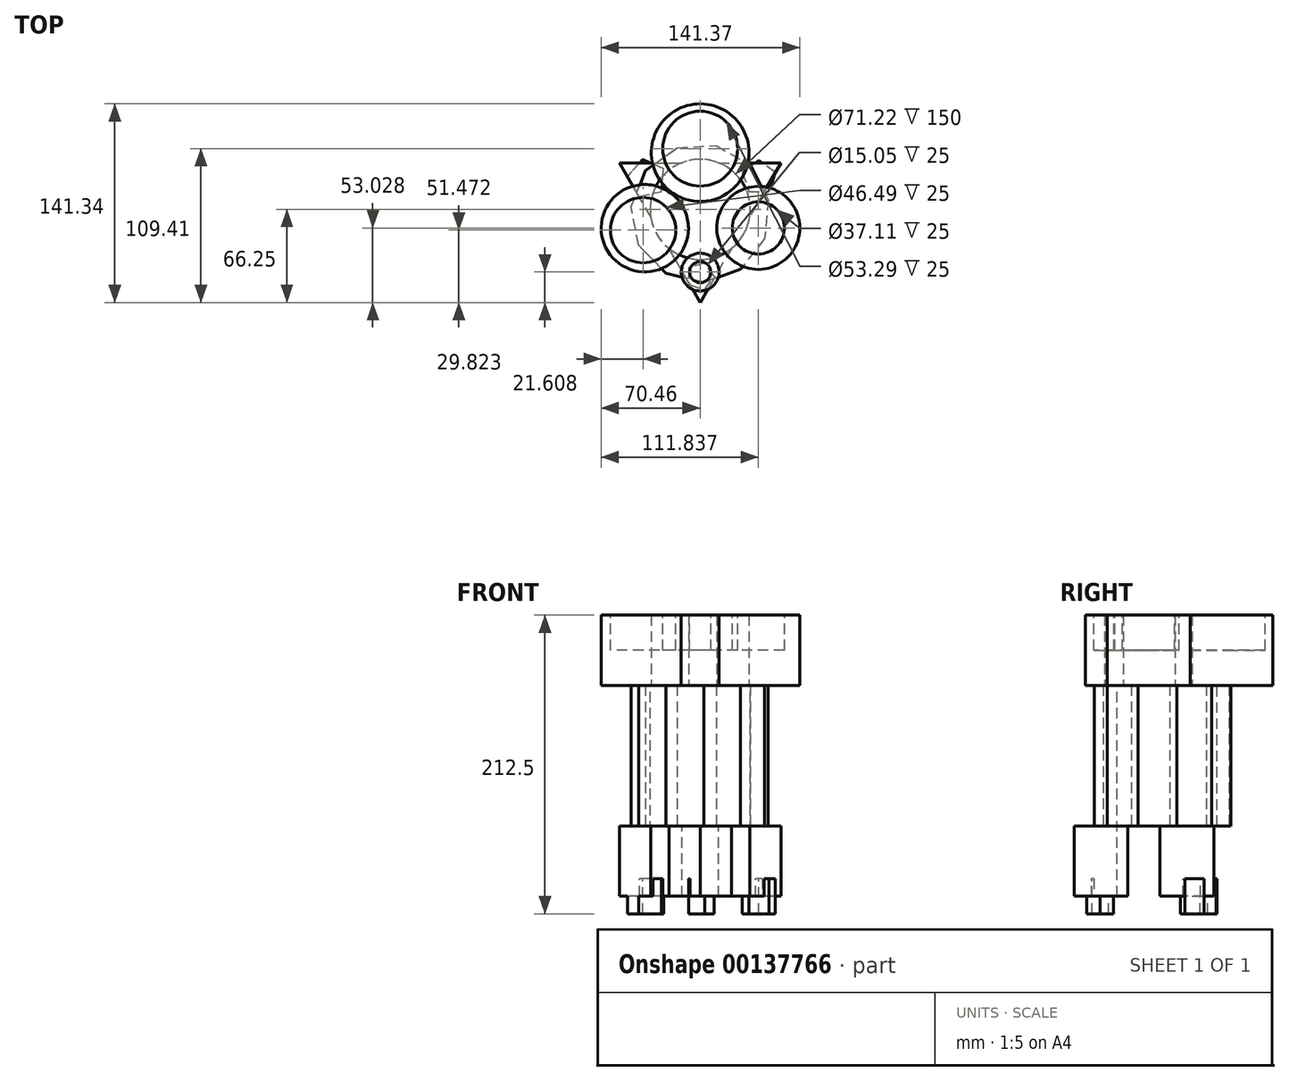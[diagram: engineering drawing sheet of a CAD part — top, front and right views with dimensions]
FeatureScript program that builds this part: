
annotation { "Feature Type Name" : "Feature", "Feature Type Description" : "" }
export const myFeature = defineFeature(function(context is Context, id is Id, definition is map)
    precondition{}
    {
        {
            var Q0;
            Q0=qCreatedBy(makeId("Top.planeOp"),FACE);
            var sketch = newSketch(context, id + "F0", { "sketchPlane" : qUnion([Q0])});
            skCircle(sketch, "E0.cCircle", {"center": v(0, 0) * mm, "radius": 33.12 * mm, "construction": true});
            skLineSegment(sketch, "E0.0", {"start": v(-57.37, 33.12) * mm, "end": v(57.37, 33.12) * mm});
            skLineSegment(sketch, "E0.1", {"start": v(57.37, 33.12) * mm, "end": v(0, -66.25) * mm});
            skLineSegment(sketch, "E0.2", {"start": v(0, -66.25) * mm, "end": v(-57.37, 33.12) * mm});
            skPoint(sketch, "E0.0.midPoint", {"position": v(0, 33.12) * mm});
            skSolve(sketch);
        }
        {
            var Q0;
            Q0 = qSketchRegion(id + "F0", true);
            extrude(context, id + "F1", {"entities" : qUnion([Q0]), "depth" : 50 * mm});
        }
        {
            var Q0;
            Q0=makeQuery(id+"F1.opExtrude","CAP_FACE",FACE,{"disambiguationData":[OSD([sQuery(id+"F0.wireOp",EDGE,"E0.0"),sQuery(id+"F0.wireOp",EDGE,"E0.1"),sQuery(id+"F0.wireOp",EDGE,"E0.2")])],"isStart":false});
            var sketch = newSketch(context, id + "F2", { "sketchPlane" : qUnion([Q0])});
            skCircle(sketch, "E1.cCircle", {"center": v(0, -2.63) * mm, "radius": 47.32 * mm, "construction": true});
            skLineSegment(sketch, "E1.0", {"start": v(11.42, 45.34) * mm, "end": v(35.54, 31.56) * mm});
            skLineSegment(sketch, "E1.1", {"start": v(35.54, 31.56) * mm, "end": v(48.38, 6.91) * mm});
            skLineSegment(sketch, "E1.2", {"start": v(48.38, 6.91) * mm, "end": v(45.86, -20.76) * mm});
            skLineSegment(sketch, "E1.3", {"start": v(45.86, -20.76) * mm, "end": v(28.78, -42.67) * mm});
            skLineSegment(sketch, "E1.4", {"start": v(28.78, -42.67) * mm, "end": v(2.56, -51.88) * mm});
            skLineSegment(sketch, "E1.5", {"start": v(2.56, -51.88) * mm, "end": v(-24.47, -45.44) * mm});
            skLineSegment(sketch, "E1.6", {"start": v(-24.47, -45.44) * mm, "end": v(-43.73, -25.42) * mm});
            skLineSegment(sketch, "E1.7", {"start": v(-43.73, -25.42) * mm, "end": v(-49.1, 1.85) * mm});
            skLineSegment(sketch, "E1.8", {"start": v(-49.1, 1.85) * mm, "end": v(-38.9, 27.69) * mm});
            skLineSegment(sketch, "E1.9", {"start": v(-38.9, 27.69) * mm, "end": v(-16.33, 43.9) * mm});
            skLineSegment(sketch, "E1.10", {"start": v(-16.33, 43.9) * mm, "end": v(11.42, 45.34) * mm});
            skPoint(sketch, "E1.0.midPoint", {"position": v(23.48, 38.45) * mm});
            skSolve(sketch);
        }
        {
            var Q0;
            Q0 = qSketchRegion(id + "F2", true);
            extrude(context, id + "F3", {"entities" : qUnion([Q0]), "operationType" : NewBodyOperationType.ADD, "depth" : 100 * mm});
        }
        {
            var Q0;
            Q0=makeQuery(id+"F3.opExtrude","CAP_FACE",FACE,{"disambiguationData":[OSD([sQuery(id+"F2.wireOp",EDGE,"E1.0"),sQuery(id+"F2.wireOp",EDGE,"E1.1"),sQuery(id+"F2.wireOp",EDGE,"E1.2"),sQuery(id+"F2.wireOp",EDGE,"E1.3"),sQuery(id+"F2.wireOp",EDGE,"E1.4"),sQuery(id+"F2.wireOp",EDGE,"E1.5"),sQuery(id+"F2.wireOp",EDGE,"E1.6"),sQuery(id+"F2.wireOp",EDGE,"E1.7"),sQuery(id+"F2.wireOp",EDGE,"E1.8"),sQuery(id+"F2.wireOp",EDGE,"E1.9"),sQuery(id+"F2.wireOp",EDGE,"E1.10")])],"isStart":false});
            var sketch = newSketch(context, id + "F4", { "sketchPlane" : qUnion([Q0])});
            skCircle(sketch, "E2", {"center": v(0, 0) * mm, "radius": 35.61 * mm});
            skSolve(sketch);
        }
        {
            var Q0;
            Q0 = qSketchRegion(id + "F4", true);
            extrude(context, id + "F5", {"entities" : qUnion([Q0]), "operationType" : NewBodyOperationType.REMOVE, "endBound" : BoundingType.THROUGH_ALL, "oppositeDirection" : true, "depth" : 25 * mm});
        }
        {
            var Q0;
            Q0=makeQuery(id+"F3.opExtrude","CAP_FACE",FACE,{"disambiguationData":[OSD([sQuery(id+"F2.wireOp",EDGE,"E1.0"),sQuery(id+"F2.wireOp",EDGE,"E1.1"),sQuery(id+"F2.wireOp",EDGE,"E1.2"),sQuery(id+"F2.wireOp",EDGE,"E1.3"),sQuery(id+"F2.wireOp",EDGE,"E1.4"),sQuery(id+"F2.wireOp",EDGE,"E1.5"),sQuery(id+"F2.wireOp",EDGE,"E1.6"),sQuery(id+"F2.wireOp",EDGE,"E1.7"),sQuery(id+"F2.wireOp",EDGE,"E1.8"),sQuery(id+"F2.wireOp",EDGE,"E1.9"),sQuery(id+"F2.wireOp",EDGE,"E1.10")])],"isStart":false});
            var sketch = newSketch(context, id + "F6", { "sketchPlane" : qUnion([Q0])});
            skCircle(sketch, "E3", {"center": v(0, 40.32) * mm, "radius": 34.76 * mm});
            skCircle(sketch, "E4", {"center": v(0, -44.64) * mm, "radius": 13.46 * mm});
            skCircle(sketch, "E5", {"center": v(41.38, -13.22) * mm, "radius": 29.53 * mm});
            skCircle(sketch, "E6", {"center": v(-39.39, -13.44) * mm, "radius": 31.07 * mm});
            skSolve(sketch);
        }
        {
            var Q0;
            Q0 = qSketchRegion(id + "F6", true);
            extrude(context, id + "F7", {"entities" : qUnion([Q0]), "operationType" : NewBodyOperationType.ADD, "depth" : 50 * mm});
        }
        {
            var Q0;
            {var subQ0=sQuery(id+"F0.wireOp",EDGE,"E0.0");var subQ1=sQuery(id+"F0.wireOp",EDGE,"E0.2");Q0=makeQuery(id+"F5.boolean.opBoolean","SPLIT",FACE,{"disambiguationData":[TD([makeQuery(id+"F1.opExtrude","SWEPT_FACE",FACE,{"disambiguationData":[OSD([subQ0])]}),makeQuery(id+"F1.opExtrude","SWEPT_FACE",FACE,{"disambiguationData":[OSD([subQ1])]}),makeQuery(id+"F5.opExtrude","SWEPT_FACE",FACE,{"disambiguationData":[OSD([sQuery(id+"F4.wireOp",EDGE,"E2")])]})])],"derivedFrom":makeQuery(id+"F1.opExtrude","CAP_FACE",FACE,{"disambiguationData":[OSD([subQ0,sQuery(id+"F0.wireOp",EDGE,"E0.1"),subQ1])],"isStart":true})});}
            var sketch = newSketch(context, id + "F8", { "sketchPlane" : qUnion([Q0])});
            skCircle(sketch, "E7.cCircle", {"center": v(-37.98, -21.98) * mm, "radius": 11.22 * mm, "construction": true});
            skLineSegment(sketch, "E7.0", {"start": v(-51.78, -23.43) * mm, "end": v(-43.62, -9.3) * mm});
            skLineSegment(sketch, "E7.1", {"start": v(-43.62, -9.3) * mm, "end": v(-27.67, -12.7) * mm});
            skLineSegment(sketch, "E7.2", {"start": v(-27.67, -12.7) * mm, "end": v(-25.96, -28.92) * mm});
            skLineSegment(sketch, "E7.3", {"start": v(-25.96, -28.92) * mm, "end": v(-40.86, -35.55) * mm});
            skLineSegment(sketch, "E7.4", {"start": v(-40.86, -35.55) * mm, "end": v(-51.78, -23.43) * mm});
            skPoint(sketch, "E7.0.midPoint", {"position": v(-47.7, -16.37) * mm});
            skCircle(sketch, "E8.cCircle", {"center": v(0, 47.58) * mm, "radius": 8.12 * mm, "construction": true});
            skLineSegment(sketch, "E8.0", {"start": v(-8.12, 41.68) * mm, "end": v(-8.12, 53.49) * mm});
            skLineSegment(sketch, "E8.1", {"start": v(-8.12, 53.49) * mm, "end": v(3.1, 57.13) * mm});
            skLineSegment(sketch, "E8.2", {"start": v(3.1, 57.13) * mm, "end": v(10.04, 47.58) * mm});
            skLineSegment(sketch, "E8.3", {"start": v(10.04, 47.58) * mm, "end": v(3.1, 38.03) * mm});
            skLineSegment(sketch, "E8.4", {"start": v(3.1, 38.03) * mm, "end": v(-8.12, 41.68) * mm});
            skPoint(sketch, "E8.0.midPoint", {"position": v(-8.12, 47.58) * mm});
            skCircle(sketch, "E9.cCircle", {"center": v(41.77, -22.56) * mm, "radius": 9.98 * mm, "construction": true});
            skLineSegment(sketch, "E9.0", {"start": v(34.52, -12.58) * mm, "end": v(49.03, -12.58) * mm});
            skLineSegment(sketch, "E9.1", {"start": v(49.03, -12.58) * mm, "end": v(53.5, -26.37) * mm});
            skLineSegment(sketch, "E9.2", {"start": v(53.5, -26.37) * mm, "end": v(41.77, -34.9) * mm});
            skLineSegment(sketch, "E9.3", {"start": v(41.77, -34.9) * mm, "end": v(30.04, -26.37) * mm});
            skLineSegment(sketch, "E9.4", {"start": v(30.04, -26.37) * mm, "end": v(34.52, -12.58) * mm});
            skPoint(sketch, "E9.0.midPoint", {"position": v(41.77, -12.58) * mm});
            skSolve(sketch);
        }
        {
            var Q0;
            Q0 = qSketchRegion(id + "F8", true);
            extrude(context, id + "F9", {"entities" : qUnion([Q0]), "operationType" : NewBodyOperationType.ADD, "endBound" : BoundingType.SYMMETRIC, "depth" : 25 * mm});
        }
        {
            var Q0;
            Q0=makeQuery(id+"F7.opExtrude","CAP_FACE",FACE,{"disambiguationData":[OSD([sQuery(id+"F6.wireOp",EDGE,"E4")])],"isStart":false});
            var sketch = newSketch(context, id + "F10", { "sketchPlane" : qUnion([Q0])});
            skCircle(sketch, "E10", {"center": v(0, -44.64) * mm, "radius": 7.52 * mm});
            skSolve(sketch);
        }
        {
            var Q0;
            Q0 = qSketchRegion(id + "F10", true);
            extrude(context, id + "F11", {"entities" : qUnion([Q0]), "operationType" : NewBodyOperationType.REMOVE, "oppositeDirection" : true, "depth" : 25 * mm});
        }
        {
            var Q0;
            Q0=makeQuery(id+"F7.opExtrude","CAP_FACE",FACE,{"disambiguationData":[OSD([sQuery(id+"F6.wireOp",EDGE,"E5")])],"isStart":false});
            var sketch = newSketch(context, id + "F12", { "sketchPlane" : qUnion([Q0])});
            skCircle(sketch, "E11", {"center": v(41.38, -13.22) * mm, "radius": 18.56 * mm});
            skCircle(sketch, "E12", {"center": v(-40.64, -14.78) * mm, "radius": 23.24 * mm});
            skCircle(sketch, "E13", {"center": v(0, 43.16) * mm, "radius": 26.65 * mm});
            skSolve(sketch);
        }
        {
            var Q0;
            Q0 = qSketchRegion(id + "F12", true);
            extrude(context, id + "F13", {"entities" : qUnion([Q0]), "operationType" : NewBodyOperationType.REMOVE, "oppositeDirection" : true, "depth" : 25 * mm});
        }
    });
